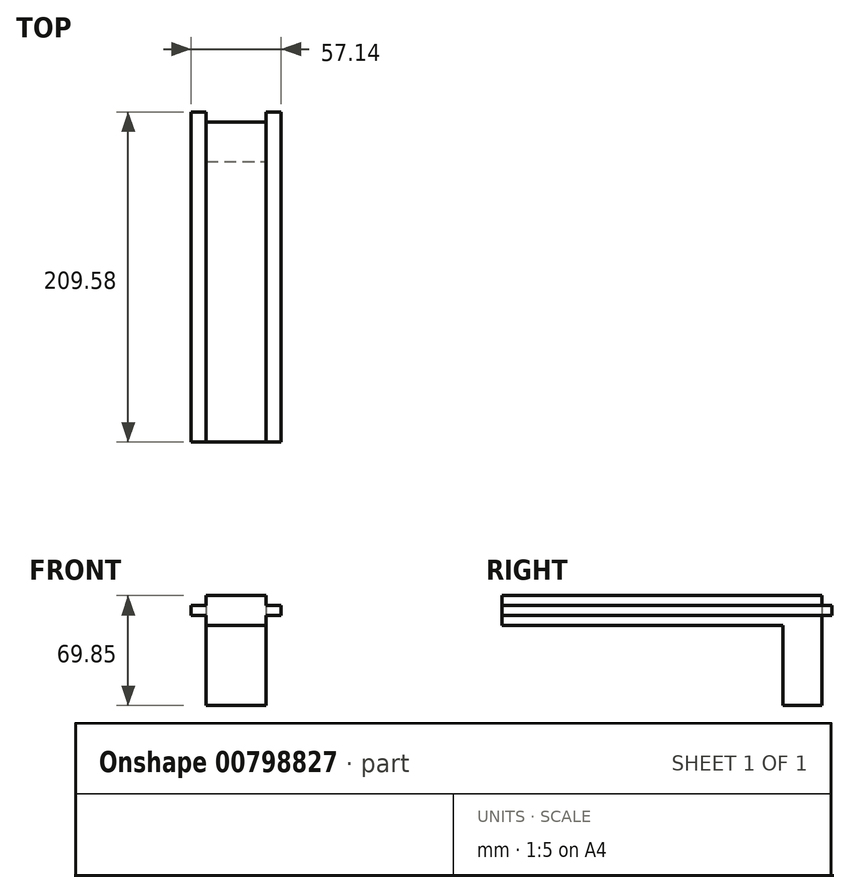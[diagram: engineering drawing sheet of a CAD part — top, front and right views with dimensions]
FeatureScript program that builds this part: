
annotation { "Feature Type Name" : "Feature", "Feature Type Description" : "" }
export const myFeature = defineFeature(function(context is Context, id is Id, definition is map)
    precondition{}
    {
        {
            var Q0;
            Q0=qCreatedBy(makeId("Front.planeOp"),FACE);
            var sketch = newSketch(context, id + "F0", { "sketchPlane" : qUnion([Q0])});
            skLineSegment(sketch, "E0.bottom", {"start": v(-19.05, 9.52) * mm, "end": v(19.05, 9.52) * mm});
            skLineSegment(sketch, "E0.top", {"start": v(-19.05, -9.53) * mm, "end": v(19.05, -9.53) * mm});
            skLineSegment(sketch, "E0.left", {"start": v(-19.05, 9.52) * mm, "end": v(-19.05, -9.53) * mm});
            skLineSegment(sketch, "E0.right", {"start": v(19.05, 9.53) * mm, "end": v(19.05, -9.52) * mm});
            skSolve(sketch);
        }
        {
            var Q0;
            Q0=makeQuery(id+"F0.imprint","IMPRINT",FACE,{"disambiguationData":[TD([[makeQuery(id+"F0.imprint","IMPRINT",EDGE,{"derivedFrom":sQuery(id+"F0.wireOp",EDGE,"E0.bottom")}),-1.0]])]});
            extrude(context, id + "F1", {"entities" : qUnion([Q0]), "depth" : 203.2 * mm, "offsetDistance" : 25.4 * mm});
        }
        {
            var Q0;
            Q0=makeQuery(id+"F1.opExtrude","CAP_FACE",FACE,{"disambiguationData":[OSD([sQuery(id+"F0.wireOp",EDGE,"E0.bottom"),sQuery(id+"F0.wireOp",EDGE,"E0.top"),sQuery(id+"F0.wireOp",EDGE,"E0.left"),sQuery(id+"F0.wireOp",EDGE,"E0.right")])],"isStart":false});
            var sketch = newSketch(context, id + "F2", { "sketchPlane" : qUnion([Q0])});
            skLineSegment(sketch, "E1.bottom", {"start": v(-19.05, 3.17) * mm, "end": v(-28.58, 3.17) * mm});
            skLineSegment(sketch, "E1.top", {"start": v(-19.05, -3.05) * mm, "end": v(-28.58, -3.05) * mm});
            skLineSegment(sketch, "E1.left", {"start": v(-19.05, 3.17) * mm, "end": v(-19.05, -3.05) * mm});
            skLineSegment(sketch, "E1.right", {"start": v(-28.58, 3.17) * mm, "end": v(-28.58, -3.05) * mm});
            skSolve(sketch);
        }
        {
            var Q0;
            Q0 = qSketchRegion(id + "F2", true);
            extrude(context, id + "F3", {"entities" : qUnion([Q0]), "endBound" : BoundingType.THROUGH_ALL, "oppositeDirection" : true, "depth" : 25.4 * mm, "offsetDistance" : 25.4 * mm});
        }
        {
            var Q0;
            Q0=makeQuery(id+"F3.opExtrude","SWEPT_BODY",BODY,{"disambiguationData":[OSD([sQuery(id+"F2.wireOp",EDGE,"E1.bottom"),sQuery(id+"F2.wireOp",EDGE,"E1.top"),sQuery(id+"F2.wireOp",EDGE,"E1.left"),sQuery(id+"F2.wireOp",EDGE,"E1.right")])]});
            var Q1;
            Q1=qCreatedBy(makeId("Right.planeOp"),FACE);
            mirror(context, id + "F4", {"operationType" : NewBodyOperationType.ADD, "entities" : qUnion([Q0]), "mirrorPlane" : qUnion([Q1])});
        }
        {
            var Q0;
            Q0=makeQuery(id+"F1.opExtrude","SWEPT_FACE",FACE,{"disambiguationData":[OSD([sQuery(id+"F0.wireOp",EDGE,"E0.top")])]});
            var sketch = newSketch(context, id + "F5", { "sketchPlane" : qUnion([Q0])});
            skLineSegment(sketch, "E2.bottom", {"start": v(-19.05, 25.02) * mm, "end": v(19.05, 25.02) * mm});
            skLineSegment(sketch, "E2.top", {"start": v(-19.05, 0) * mm, "end": v(19.05, 0) * mm});
            skLineSegment(sketch, "E2.left", {"start": v(-19.05, 25.02) * mm, "end": v(-19.05, 0) * mm});
            skLineSegment(sketch, "E2.right", {"start": v(19.05, 25.02) * mm, "end": v(19.05, 0) * mm});
            skSolve(sketch);
        }
        {
            var Q0;
            Q0 = qSketchRegion(id + "F5", true);
            extrude(context, id + "F6", {"entities" : qUnion([Q0]), "operationType" : NewBodyOperationType.ADD, "depth" : 50.8 * mm, "offsetDistance" : 25.4 * mm});
        }
    });
